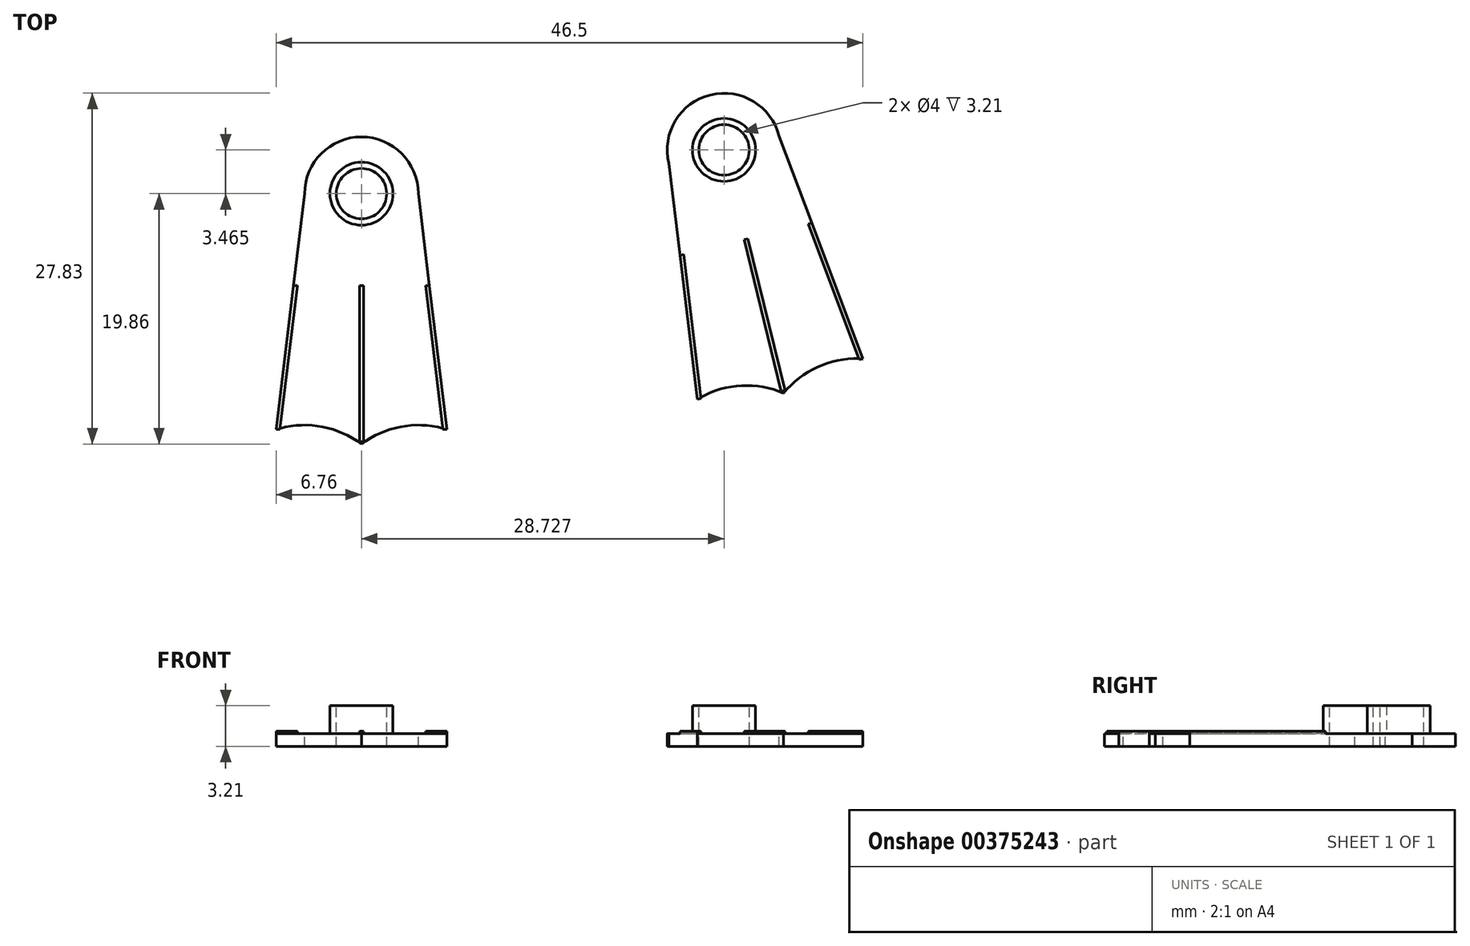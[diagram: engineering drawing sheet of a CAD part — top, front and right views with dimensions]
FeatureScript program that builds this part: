
annotation { "Feature Type Name" : "Feature", "Feature Type Description" : "" }
export const myFeature = defineFeature(function(context is Context, id is Id, definition is map)
    precondition{}
    {
        {
            var Q0;
            Q0=qCreatedBy(makeId("Top.planeOp"),FACE);
            var sketch = newSketch(context, id + "F0", { "sketchPlane" : qUnion([Q0])});
            skCircle(sketch, "E0", {"center": v(0, 0) * mm, "radius": 2.5 * mm});
            skSolve(sketch);
        }
        {
            var Q0;
            Q0=makeQuery(id+"F0.imprint","IMPRINT",FACE,{"disambiguationData":[TD([[makeQuery(id+"F0.imprint","IMPRINT",EDGE,{"derivedFrom":sQuery(id+"F0.wireOp",EDGE,"E0")}),1.0]])]});
            extrude(context, id + "F1", {"entities" : qUnion([Q0]), "depth" : 2.2 * mm});
        }
        {
            var Q0;
            Q0=makeQuery(id+"F1.opExtrude","CAP_FACE",FACE,{"disambiguationData":[OSD([sQuery(id+"F0.wireOp",EDGE,"E0")])],"isStart":true});
            var sketch = newSketch(context, id + "F2", { "sketchPlane" : qUnion([Q0])});
            skCircle(sketch, "E1", {"center": v(0, 0) * mm, "radius": 4.5 * mm});
            skLineSegment(sketch, "E2", {"start": v(-4.5, 0) * mm, "end": v(-6.9, 19.86) * mm});
            skLineSegment(sketch, "E3", {"start": v(4.5, 0) * mm, "end": v(6.9, 19.86) * mm});
            skLineSegment(sketch, "E4", {"start": v(-6.9, 19.86) * mm, "end": v(6.9, 19.86) * mm});
            skLineSegment(sketch, "E5", {"start": v(0, 0) * mm, "end": v(0, 19.86) * mm, "construction": true});
            skSolve(sketch);
        }
        {
            var Q0;
            Q0=qSketchRegion(id+"F2",true);
            extrude(context, id + "F3", {"entities" : qUnion([Q0]), "operationType" : NewBodyOperationType.ADD, "depth" : 1 * mm});
        }
        {
            var Q0;
            Q0=makeQuery(id+"F1.opExtrude","CAP_FACE",FACE,{"disambiguationData":[OSD([sQuery(id+"F0.wireOp",EDGE,"E0")])],"isStart":false});
            var sketch = newSketch(context, id + "F4", { "sketchPlane" : qUnion([Q0])});
            skCircle(sketch, "E6", {"center": v(0, 0) * mm, "radius": 2 * mm});
            skSolve(sketch);
        }
        {
            var Q0;
            Q0=makeQuery(id+"F4.imprint","IMPRINT",FACE,{"disambiguationData":[TD([[makeQuery(id+"F4.imprint","IMPRINT",EDGE,{"derivedFrom":sQuery(id+"F4.wireOp",EDGE,"E6")}),1.0]])]});
            extrude(context, id + "F5", {"entities" : qUnion([Q0]), "operationType" : NewBodyOperationType.REMOVE, "oppositeDirection" : true, "depth" : 25 * mm});
        }
        {
            var Q0;
            {var subQ0=sQuery(id+"F2.wireOp",EDGE,"E2");Q0=makeQuery(id+"F2.imprint","IMPRINT",FACE,{"disambiguationData":[TD([[makeQuery(id+"F2.imprint","IMPRINT",EDGE,{"derivedFrom":subQ0}),-1.0]])]});}
            var sketch = newSketch(context, id + "F6", { "sketchPlane" : qUnion([Q0])});
            skCircle(sketch, "E7", {"center": v(-4.5, 25.85) * mm, "radius": 7.5 * mm});
            skCircle(sketch, "E8", {"center": v(4.5, 25.85) * mm, "radius": 7.5 * mm});
            skSolve(sketch);
        }
        {
            var Q0;
            Q0=qSketchRegion(id+"F6",true);
            extrude(context, id + "F7", {"entities" : qUnion([Q0]), "operationType" : NewBodyOperationType.REMOVE, "depth" : 25 * mm});
        }
        {
            var Q0;
            {var subQ0=sQuery(id+"F2.wireOp",EDGE,"E2");Q0=makeQuery(id+"F2.imprint","IMPRINT",FACE,{"disambiguationData":[TD([[makeQuery(id+"F2.imprint","IMPRINT",EDGE,{"derivedFrom":subQ0}),-1.0]])]});}
            var sketch = newSketch(context, id + "F8", { "sketchPlane" : qUnion([Q0])});
            skLineSegment(sketch, "E9", {"start": v(-5.38, 7.3) * mm, "end": v(-6.76, 18.7) * mm});
            skLineSegment(sketch, "E10", {"start": v(-5.38, 7.3) * mm, "end": v(5.08, 7.3) * mm, "construction": true});
            skLineSegment(sketch, "E11", {"start": v(-6.76, 18.7) * mm, "end": v(-6.46, 18.7) * mm});
            skLineSegment(sketch, "E12", {"start": v(-6.46, 18.7) * mm, "end": v(-5.08, 7.3) * mm});
            skLineSegment(sketch, "E13", {"start": v(-5.08, 7.3) * mm, "end": v(-5.38, 7.3) * mm});
            skLineSegment(sketch, "E14", {"start": v(5.38, 7.3) * mm, "end": v(6.76, 18.7) * mm});
            skLineSegment(sketch, "E15", {"start": v(5.38, 7.3) * mm, "end": v(5.08, 7.3) * mm});
            skLineSegment(sketch, "E16", {"start": v(5.08, 7.3) * mm, "end": v(6.46, 18.7) * mm});
            skLineSegment(sketch, "E17", {"start": v(6.46, 18.7) * mm, "end": v(6.76, 18.7) * mm});
            skLineSegment(sketch, "E18", {"start": v(0, 7.3) * mm, "end": v(0, 24.68) * mm, "construction": true});
            skLineSegment(sketch, "E19", {"start": v(-0.15, 7.3) * mm, "end": v(-0.15, 19.67) * mm});
            skLineSegment(sketch, "E20", {"start": v(-0.15, 19.67) * mm, "end": v(0.15, 19.67) * mm});
            skLineSegment(sketch, "E21", {"start": v(0.15, 19.67) * mm, "end": v(0.15, 7.3) * mm});
            skLineSegment(sketch, "E22", {"start": v(0.15, 7.3) * mm, "end": v(-0.15, 7.3) * mm});
            skSolve(sketch);
        }
        {
            var Q0;
            Q0=qSketchRegion(id+"F8",true);
            extrude(context, id + "F9", {"entities" : qUnion([Q0]), "operationType" : NewBodyOperationType.ADD, "oppositeDirection" : true, "depth" : .2 * mm});
        }
        {
            var Q0;
            Q0=makeQuery(id+"F9.boolean.opBoolean","MERGE",FACE,{"derivedFrom":[makeQuery(id+"F3.opExtrude","SWEPT_FACE",FACE,{"disambiguationData":[OSD([sQuery(id+"F2.wireOp",EDGE,"E3")])]}),makeQuery(id+"F9.opExtrude","SWEPT_FACE",FACE,{"disambiguationData":[OSD([sQuery(id+"F8.wireOp",EDGE,"E14")])]})]});
            cPlane(context, id + "F10", {"entities" : qUnion([Q0]), "cplaneType" : CPlaneType.OFFSET, "offset" : 10 * mm, "width" : 150 * mm, "height" : 150 * mm});
        }
        {
            var Q0;
            Q0=makeQuery(id+"F1.opExtrude","SWEPT_BODY",BODY,{"disambiguationData":[OSD([sQuery(id+"F0.wireOp",EDGE,"E0")])]});
            var Q1;
            Q1=qCreatedBy(id+"F10.planeOp",FACE);
            mirror(context, id + "F11", {"entities" : qUnion([Q0]), "mirrorPlane" : qUnion([Q1])});
        }
    });
